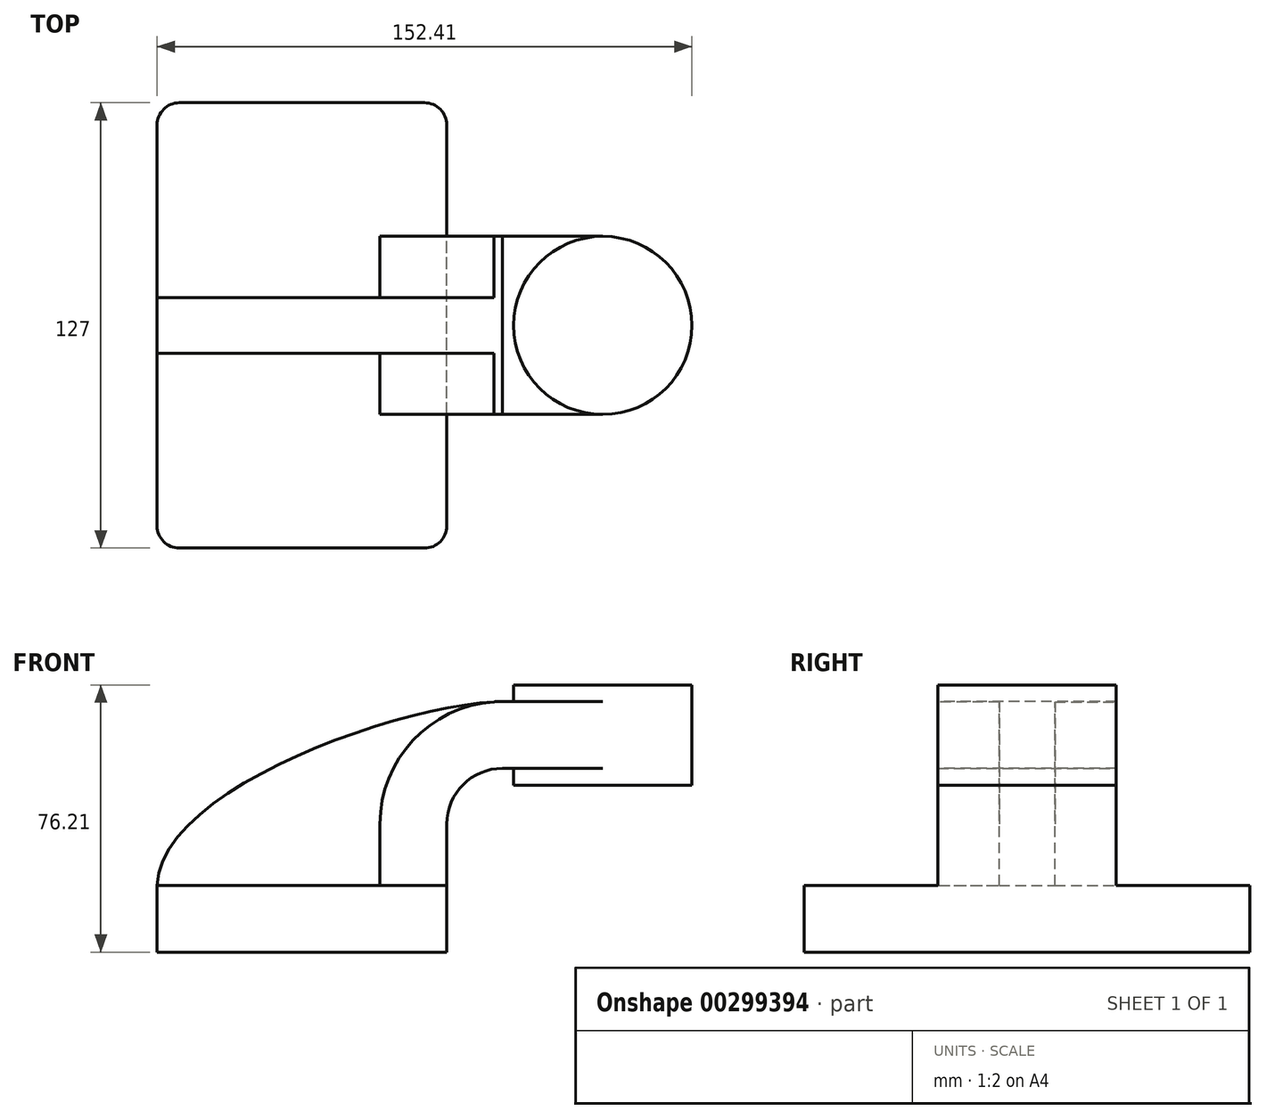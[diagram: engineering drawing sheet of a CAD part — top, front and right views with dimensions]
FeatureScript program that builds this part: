
annotation { "Feature Type Name" : "Feature", "Feature Type Description" : "" }
export const myFeature = defineFeature(function(context is Context, id is Id, definition is map)
    precondition{}
    {
        {
            var Q0;
            Q0=qCreatedBy(makeId("Front.planeOp"),FACE);
            var sketch = newSketch(context, id + "F0", { "sketchPlane" : qUnion([Q0])});
            skLineSegment(sketch, "E0.bottom", {"start": v(-41.28, 9.52) * mm, "end": v(41.27, 9.53) * mm});
            skLineSegment(sketch, "E0.top", {"start": v(-41.28, -9.53) * mm, "end": v(41.28, -9.53) * mm});
            skLineSegment(sketch, "E0.left", {"start": v(-41.28, 9.52) * mm, "end": v(-41.27, -9.53) * mm});
            skLineSegment(sketch, "E0.right", {"start": v(41.28, 9.53) * mm, "end": v(41.28, -9.52) * mm});
            skPoint(sketch, "E0.middle", {"position": v(0, 0) * mm});
            skLineSegment(sketch, "E1", {"start": v(41.27, 9.53) * mm, "end": v(41.27, 27) * mm});
            skArc(sketch, "E2", {"start": v(41.27, 27) * mm, "mid": v(45.92, 38.23) * mm, "end": v(57.15, 42.88) * mm});
            skLineSegment(sketch, "E3.bottom", {"start": v(111.12, 38.1) * mm, "end": v(60.32, 38.1) * mm});
            skLineSegment(sketch, "E3.top", {"start": v(111.12, 66.68) * mm, "end": v(60.32, 66.68) * mm});
            skLineSegment(sketch, "E3.left", {"start": v(111.12, 38.1) * mm, "end": v(111.12, 66.68) * mm});
            skLineSegment(sketch, "E3.right", {"start": v(60.32, 38.1) * mm, "end": v(60.32, 66.68) * mm});
            skPoint(sketch, "E3.middle", {"position": v(85.72, 52.39) * mm});
            skPoint(sketch, "E4.endSnap0", {"position": v(85.72, 38.1) * mm});
            skLineSegment(sketch, "E5", {"start": v(57.15, 42.88) * mm, "end": v(85.72, 42.88) * mm});
            skLineSegment(sketch, "E6.0", {"start": v(57.15, 61.93) * mm, "end": v(85.72, 61.93) * mm});
            skArc(sketch, "E6.1", {"start": v(22.22, 27) * mm, "mid": v(32.45, 51.7) * mm, "end": v(57.15, 61.93) * mm});
            skLineSegment(sketch, "E6.2", {"start": v(22.22, 9.53) * mm, "end": v(22.22, 27) * mm});
            skLineSegment(sketch, "E7", {"start": v(85.72, 66.68) * mm, "end": v(85.72, 38.1) * mm});
            skFitSpline(sketch, "E8", {"points": [v(-41.28, 9.52) * mm, v(57.15, 61.93) * mm], "startDerivative": vector(2.17, 83.8) * mm, "endDerivative": vector(82.74, 1.02) * mm});
            skSolve(sketch);
        }
        {
            var Q0;
            Q0=makeQuery(id+"F0.imprint","IMPRINT",FACE,{"disambiguationData":[TD([[makeQuery(id+"F0.imprint","IMPRINT",EDGE,{"derivedFrom":sQuery(id+"F0.wireOp",EDGE,"E0.top")}),1.0]])]});
            extrude(context, id + "F1", {"entities" : qUnion([Q0]), "endBound" : BoundingType.SYMMETRIC, "depth" : 127 * mm});
        }
        {
            var Q0;
            {var subQ5=sQuery(id+"F0.wireOp",EDGE,"E1");Q0=makeQuery(id+"F0.imprint","IMPRINT",FACE,{"disambiguationData":[TD([[makeQuery(id+"F0.imprint","IMPRINT",EDGE,{"derivedFrom":subQ5}),1.0]])]});}
            var Q1;
            {var subQ0=sQuery(id+"F0.wireOp",EDGE,"E5");var subQ1=sQuery(id+"F0.wireOp",EDGE,"E3.right");var subQ2=makeQuery(id+"F0.imprint","INTERSECT",VERTEX,{"derivedFrom":[subQ1,subQ0]});Q1=makeQuery(id+"F0.imprint","IMPRINT",FACE,{"disambiguationData":[TD([[makeQuery(id+"F0.imprint","IMPRINT",EDGE,{"disambiguationData":[TD([[subQ2,-1.0]])],"derivedFrom":subQ1}),-1.0]])]});}
            extrude(context, id + "F2", {"entities" : qUnion([Q0, Q1]), "operationType" : NewBodyOperationType.ADD, "endBound" : BoundingType.SYMMETRIC, "depth" : 50.8 * mm});
        }
        {
            var Q0;
            {var subQ3=sQuery(id+"F0.wireOp",EDGE,"E6.2");Q0=makeQuery(id+"F0.imprint","IMPRINT",FACE,{"disambiguationData":[TD([[makeQuery(id+"F0.imprint","IMPRINT",EDGE,{"derivedFrom":subQ3}),1.0]])]});}
            extrude(context, id + "F3", {"entities" : qUnion([Q0]), "operationType" : NewBodyOperationType.ADD, "endBound" : BoundingType.SYMMETRIC, "depth" : 15.88 * mm});
        }
        {
            var Q0;
            {var subQ0=sQuery(id+"F0.wireOp",EDGE,"E3.left");Q0=makeQuery(id+"F0.imprint","IMPRINT",FACE,{"disambiguationData":[TD([[makeQuery(id+"F0.imprint","IMPRINT",EDGE,{"derivedFrom":subQ0}),1.0]])]});}
            var Q1;
            Q1=sQuery(id+"F0.wireOp",EDGE,"E7");
            revolve(context, id + "F4", {"operationType" : NewBodyOperationType.ADD, "entities" : qUnion([Q0]), "axis" : qUnion([Q1]), "revolveType" : RevolveType.FULL});
        }
        {
            var Q0;
            Q0=makeQuery(id+"F1.opExtrude","CAP_EDGE",EDGE,{"disambiguationData":[OSD([sQuery(id+"F0.wireOp",EDGE,"E0.right")])],"isStart":false});
            var Q1;
            Q1=makeQuery(id+"F1.opExtrude","CAP_EDGE",EDGE,{"disambiguationData":[OSD([sQuery(id+"F0.wireOp",EDGE,"E0.right")])],"isStart":true});
            var Q2;
            Q2=makeQuery(id+"F1.opExtrude","CAP_EDGE",EDGE,{"disambiguationData":[OSD([sQuery(id+"F0.wireOp",EDGE,"E0.left")])],"isStart":false});
            var Q3;
            Q3=makeQuery(id+"F1.opExtrude","CAP_EDGE",EDGE,{"disambiguationData":[OSD([sQuery(id+"F0.wireOp",EDGE,"E0.left")])],"isStart":true});
            fillet(context, id + "F5", {"entities" : qUnion([Q0, Q1, Q2, Q3]), "radius" : 6.35 * mm, "tangentPropagation" : true, "allowEdgeOverflow" : false});
        }
    });
